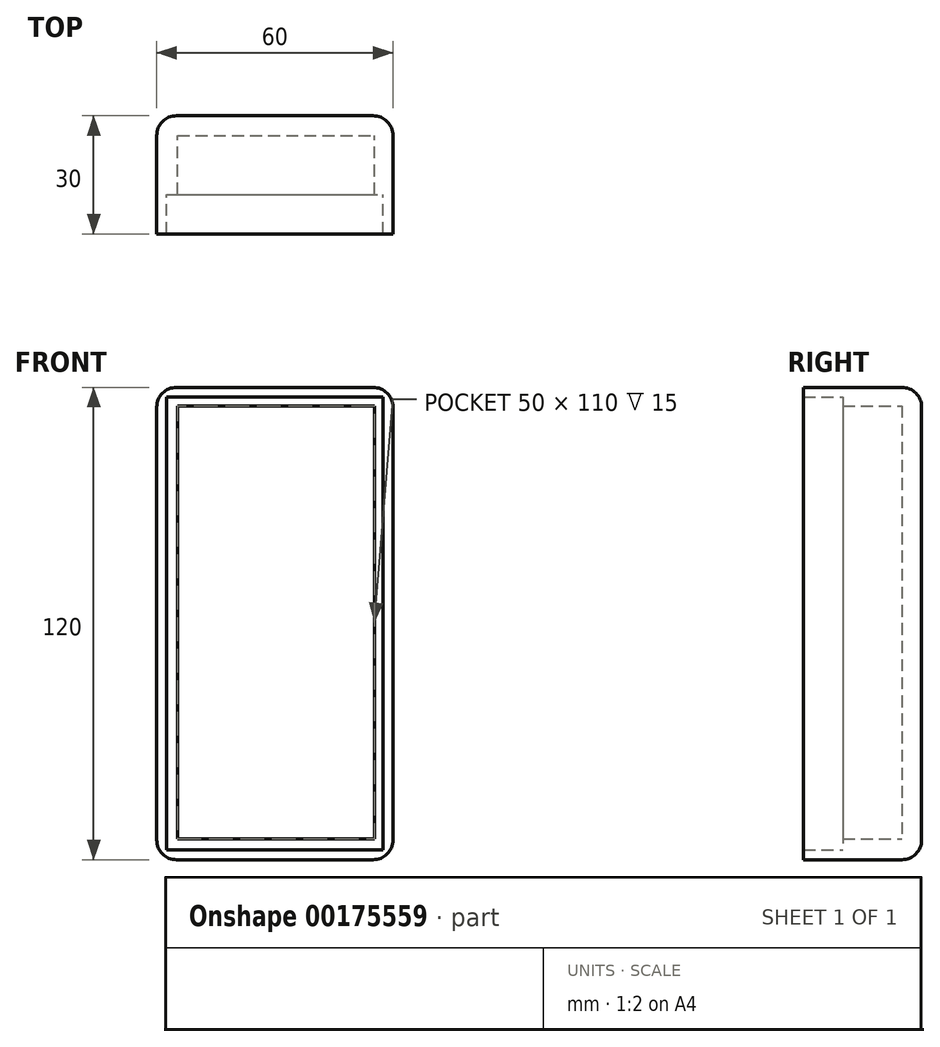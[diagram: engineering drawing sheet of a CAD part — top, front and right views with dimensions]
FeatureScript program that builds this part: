
annotation { "Feature Type Name" : "Feature", "Feature Type Description" : "" }
export const myFeature = defineFeature(function(context is Context, id is Id, definition is map)
    precondition{}
    {
        {
            var Q0;
            Q0=qCreatedBy(makeId("Front.planeOp"),FACE);
            var sketch = newSketch(context, id + "F0", { "sketchPlane" : qUnion([Q0])});
            skLineSegment(sketch, "E0.bottom", {"start": v(-23.82, 86.1) * mm, "end": v(36.18, 86.1) * mm});
            skLineSegment(sketch, "E0.top", {"start": v(-23.82, -33.9) * mm, "end": v(36.18, -33.9) * mm});
            skLineSegment(sketch, "E0.left", {"start": v(-23.82, 86.1) * mm, "end": v(-23.82, -33.9) * mm});
            skLineSegment(sketch, "E0.right", {"start": v(36.18, 86.1) * mm, "end": v(36.18, -33.9) * mm});
            skSolve(sketch);
        }
        {
            var Q0;
            Q0=makeQuery(id+"F0.imprint","IMPRINT",FACE,{"disambiguationData":[TD([[makeQuery(id+"F0.imprint","IMPRINT",EDGE,{"derivedFrom":sQuery(id+"F0.wireOp",EDGE,"E0.bottom")}),-1.0]])]});
            var sketch = newSketch(context, id + "F1", { "sketchPlane" : qUnion([Q0])});
            skLineSegment(sketch, "E1.bottom", {"start": v(-18.5, 81.44) * mm, "end": v(31.5, 81.44) * mm});
            skLineSegment(sketch, "E1.top", {"start": v(-18.5, -28.56) * mm, "end": v(31.5, -28.56) * mm});
            skLineSegment(sketch, "E1.left", {"start": v(-18.5, 81.44) * mm, "end": v(-18.5, -28.56) * mm});
            skLineSegment(sketch, "E1.right", {"start": v(31.5, 81.44) * mm, "end": v(31.5, -28.56) * mm});
            skLineSegment(sketch, "E2.bottom", {"start": v(-21.36, 83.92) * mm, "end": v(33.64, 83.92) * mm});
            skLineSegment(sketch, "E2.top", {"start": v(-21.36, -31.08) * mm, "end": v(33.64, -31.08) * mm});
            skLineSegment(sketch, "E2.left", {"start": v(-21.36, 83.92) * mm, "end": v(-21.36, -31.08) * mm});
            skLineSegment(sketch, "E2.right", {"start": v(33.64, 83.92) * mm, "end": v(33.64, -31.08) * mm});
            skSolve(sketch);
        }
        {
            var Q0;
            Q0=makeQuery(id+"F1.imprint","IMPRINT",FACE,{"disambiguationData":[TD([[makeQuery(id+"F1.imprint","IMPRINT",EDGE,{"derivedFrom":sQuery(id+"F1.wireOp",EDGE,"E2.bottom")}),1.0]])]});
            var Q1;
            Q1=makeQuery(id+"F1.imprint","IMPRINT",FACE,{"disambiguationData":[TD([[makeQuery(id+"F1.imprint","IMPRINT",EDGE,{"derivedFrom":sQuery(id+"F1.wireOp",EDGE,"E1.bottom")}),1.0]])]});
            extrude(context, id + "F2", {"entities" : qUnion([Q0, Q1]), "depth" : 20 * mm});
        }
        {
            var Q0;
            Q0=makeQuery(id+"F2.opExtrude","CAP_FACE",FACE,{"disambiguationData":[OSD([sQuery(id+"F0.wireOp",EDGE,"E0.bottom"),sQuery(id+"F0.wireOp",EDGE,"E0.top"),sQuery(id+"F0.wireOp",EDGE,"E0.left"),sQuery(id+"F0.wireOp",EDGE,"E0.right"),sQuery(id+"F1.wireOp",EDGE,"E1.bottom"),sQuery(id+"F1.wireOp",EDGE,"E1.top"),sQuery(id+"F1.wireOp",EDGE,"E1.left"),sQuery(id+"F1.wireOp",EDGE,"E1.right")])],"isStart":false});
            var sketch = newSketch(context, id + "F3", { "sketchPlane" : qUnion([Q0])});
            skLineSegment(sketch, "E3", {"start": v(-23.82, 86.1) * mm, "end": v(-23.82, 83.6) * mm});
            skLineSegment(sketch, "E4", {"start": v(-23.82, 83.6) * mm, "end": v(-21.32, 83.6) * mm});
            skLineSegment(sketch, "E5.bottom", {"start": v(-21.32, 83.6) * mm, "end": v(33.68, 83.6) * mm});
            skLineSegment(sketch, "E5.top", {"start": v(-21.32, -31.4) * mm, "end": v(33.68, -31.4) * mm});
            skLineSegment(sketch, "E5.left", {"start": v(-21.32, 83.6) * mm, "end": v(-21.32, -31.4) * mm});
            skLineSegment(sketch, "E5.right", {"start": v(33.68, 83.6) * mm, "end": v(33.68, -31.4) * mm});
            skSolve(sketch);
        }
        {
            var Q0;
            {var subQ0=sQuery(id+"F3.wireOp",EDGE,"E3");Q0=makeQuery(id+"F3.imprint","IMPRINT",FACE,{"disambiguationData":[TD([[makeQuery(id+"F3.imprint","IMPRINT",EDGE,{"derivedFrom":subQ0}),1.0]])]});}
            var sketch = newSketch(context, id + "F4", { "sketchPlane" : qUnion([Q0])});
            skSolve(sketch);
        }
        {
            var Q0;
            Q0 = qSketchRegion(id + "F4", true);
            var Q1;
            {var subQ0=sQuery(id+"F3.wireOp",EDGE,"E3");Q1=makeQuery(id+"F3.imprint","IMPRINT",FACE,{"disambiguationData":[TD([[makeQuery(id+"F3.imprint","IMPRINT",EDGE,{"derivedFrom":subQ0}),1.0]])]});}
            extrude(context, id + "F5", {"entities" : qUnion([Q0, Q1]), "operationType" : NewBodyOperationType.ADD, "depth" : 10 * mm});
        }
        {
            var Q0;
            Q0=makeQuery(id+"F0.imprint","IMPRINT",FACE,{"disambiguationData":[TD([[makeQuery(id+"F0.imprint","IMPRINT",EDGE,{"derivedFrom":sQuery(id+"F0.wireOp",EDGE,"E0.bottom")}),-1.0]])]});
            extrude(context, id + "F6", {"entities" : qUnion([Q0]), "operationType" : NewBodyOperationType.ADD, "depth" : 5 * mm});
        }
        {
            var Q0;
            {var subQ0=sQuery(id+"F0.wireOp",EDGE,"E0.right");var subQ1=sQuery(id+"F0.wireOp",EDGE,"E0.bottom");Q0=makeQuery(id+"F5.boolean.opBoolean","MERGE",EDGE,{"derivedFrom":[makeQuery(id+"F2.opExtrude","SWEPT_EDGE",EDGE,{"disambiguationData":[OSD([subQ1,subQ0])]}),makeQuery(id+"F5.opExtrude","SWEPT_EDGE",EDGE,{"disambiguationData":[OSD([subQ1,subQ0])]})]});}
            var Q1;
            Q1=makeQuery(id+"F2.opExtrude","CAP_EDGE",EDGE,{"disambiguationData":[OSD([sQuery(id+"F0.wireOp",EDGE,"E0.right")])],"isStart":true});
            var Q2;
            Q2=makeQuery(id+"F2.opExtrude","CAP_EDGE",EDGE,{"disambiguationData":[OSD([sQuery(id+"F0.wireOp",EDGE,"E0.bottom")])],"isStart":true});
            var Q3;
            {var subQ0=sQuery(id+"F0.wireOp",EDGE,"E0.bottom");Q3=makeQuery(id+"F5.boolean.opBoolean","MERGE",EDGE,{"derivedFrom":[makeQuery(id+"F2.opExtrude","SWEPT_EDGE",EDGE,{"disambiguationData":[OSD([subQ0,sQuery(id+"F0.wireOp",EDGE,"E0.left")])]}),makeQuery(id+"F5.opExtrude","SWEPT_EDGE",EDGE,{"disambiguationData":[OSD([subQ0,sQuery(id+"F3.wireOp",EDGE,"E3")])]})]});}
            var Q4;
            Q4=makeQuery(id+"F2.opExtrude","CAP_EDGE",EDGE,{"disambiguationData":[OSD([sQuery(id+"F0.wireOp",EDGE,"E0.left")])],"isStart":true});
            var Q5;
            Q5=makeQuery(id+"F2.opExtrude","CAP_EDGE",EDGE,{"disambiguationData":[OSD([sQuery(id+"F0.wireOp",EDGE,"E0.top")])],"isStart":true});
            var Q6;
            {var subQ0=sQuery(id+"F0.wireOp",EDGE,"E0.right");var subQ1=sQuery(id+"F0.wireOp",EDGE,"E0.top");Q6=makeQuery(id+"F5.boolean.opBoolean","MERGE",EDGE,{"derivedFrom":[makeQuery(id+"F2.opExtrude","SWEPT_EDGE",EDGE,{"disambiguationData":[OSD([subQ1,subQ0])]}),makeQuery(id+"F5.opExtrude","SWEPT_EDGE",EDGE,{"disambiguationData":[OSD([subQ1,subQ0])]})]});}
            var Q7;
            {var subQ0=sQuery(id+"F0.wireOp",EDGE,"E0.left");var subQ1=sQuery(id+"F0.wireOp",EDGE,"E0.top");Q7=makeQuery(id+"F5.boolean.opBoolean","MERGE",EDGE,{"derivedFrom":[makeQuery(id+"F2.opExtrude","SWEPT_EDGE",EDGE,{"disambiguationData":[OSD([subQ1,subQ0])]}),makeQuery(id+"F5.opExtrude","SWEPT_EDGE",EDGE,{"disambiguationData":[OSD([subQ1,subQ0])]})]});}
            fillet(context, id + "F7", {"entities" : qUnion([Q0, Q1, Q2, Q3, Q4, Q5, Q6, Q7]), "radius" : 5 * mm, "tangentPropagation" : true, "allowEdgeOverflow" : false});
        }
    });
